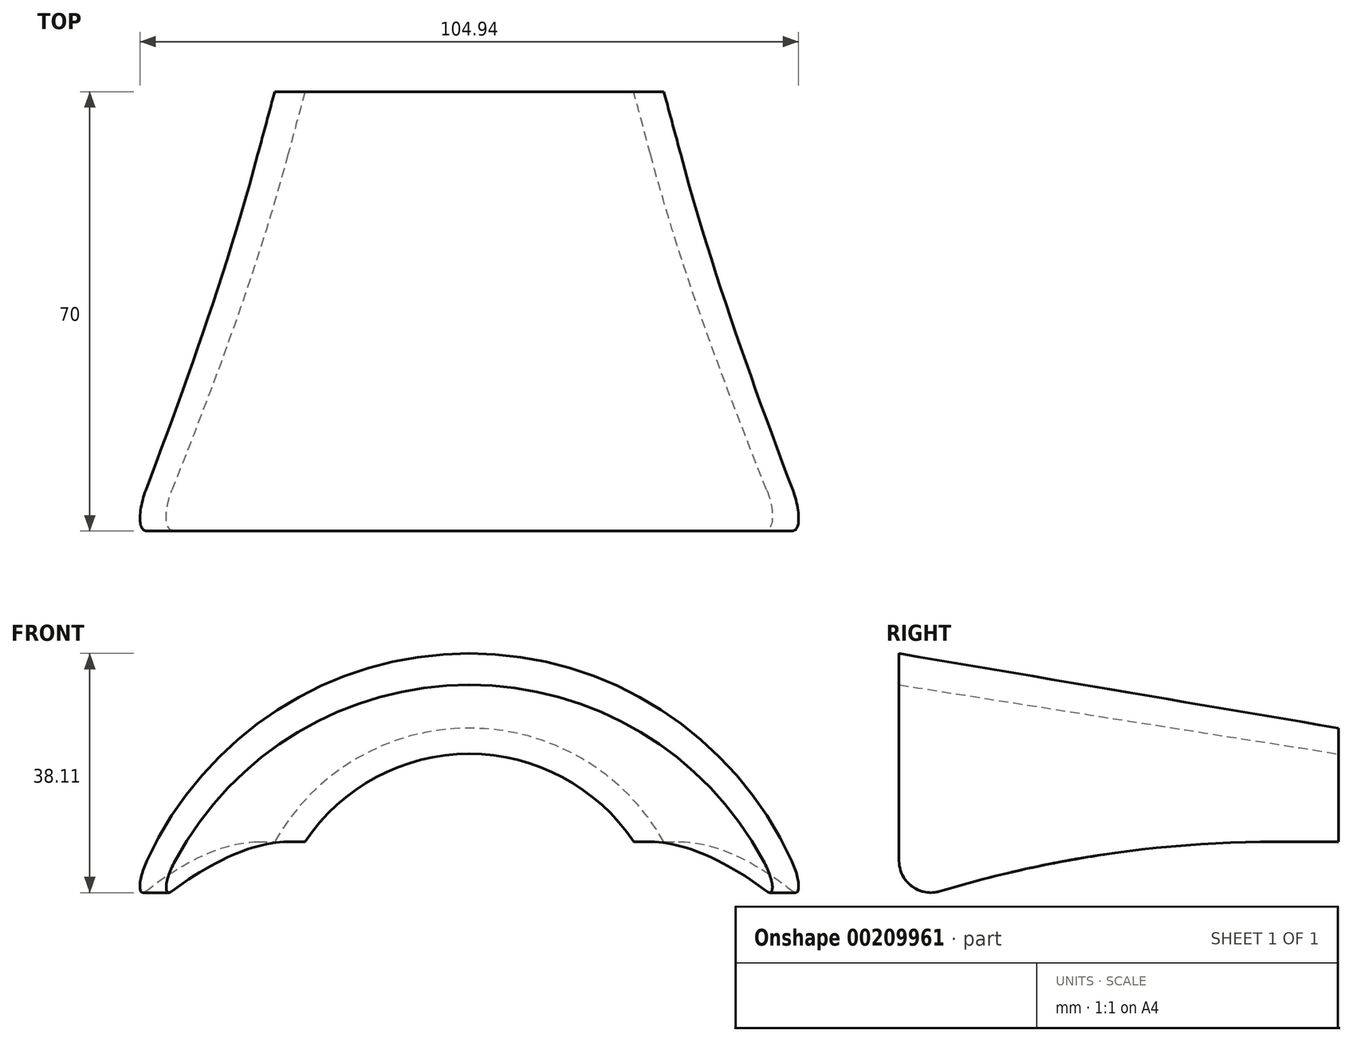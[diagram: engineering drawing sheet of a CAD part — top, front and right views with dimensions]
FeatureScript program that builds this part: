
annotation { "Feature Type Name" : "Feature", "Feature Type Description" : "" }
export const myFeature = defineFeature(function(context is Context, id is Id, definition is map)
    precondition{}
    {
        {
            var Q0;
            Q0=qCreatedBy(makeId("Front.planeOp"),FACE);
            cPlane(context, id + "F0", {"entities" : qUnion([Q0]), "cplaneType" : CPlaneType.OFFSET, "offset" : 35 * mm, "width" : 152.4 * mm, "height" : 152.4 * mm});
        }
        {
            var Q0;
            Q0=qCreatedBy(id+"F0.planeOp",FACE);
            var sketch = newSketch(context, id + "F1", { "sketchPlane" : qUnion([Q0])});
            skCircle(sketch, "E0", {"center": v(0, 0) * mm, "radius": 26.6 * mm, "construction": true});
            skLineSegment(sketch, "E1", {"start": v(-50, 0) * mm, "end": v(-54, 0) * mm});
            skLineSegment(sketch, "E2", {"start": v(50, 0) * mm, "end": v(54, 0) * mm});
            skArc(sketch, "E3", {"start": v(50, 0) * mm, "mid": v(0, 35) * mm, "end": v(-50, 0) * mm});
            skLineSegment(sketch, "E4", {"start": v(0, 0) * mm, "end": v(0, 35) * mm, "construction": true});
            skArc(sketch, "E5", {"start": v(54, 0) * mm, "mid": v(0, 40) * mm, "end": v(-54, 0) * mm});
            skLineSegment(sketch, "E6", {"start": v(0, 40) * mm, "end": v(0, 35) * mm, "construction": true});
            skSolve(sketch);
        }
        {
            var Q0;
            Q0=qCreatedBy(makeId("Front.planeOp"),FACE);
            cPlane(context, id + "F2", {"entities" : qUnion([Q0]), "cplaneType" : CPlaneType.OFFSET, "offset" : 35 * mm, "oppositeDirection" : true, "width" : 152.4 * mm, "height" : 152.4 * mm});
        }
        {
            var Q0;
            Q0=qCreatedBy(id+"F2.planeOp",FACE);
            var sketch = newSketch(context, id + "F3", { "sketchPlane" : qUnion([Q0])});
            skArc(sketch, "E7", {"start": v(26.6, 0) * mm, "mid": v(0, 26.6) * mm, "end": v(-26.6, 0) * mm, "construction": true});
            skCircle(sketch, "E8", {"center": v(0, 0) * mm, "radius": 45 * mm, "construction": true});
            skArc(sketch, "E9", {"start": v(30.6, 0) * mm, "mid": v(0, 30.6) * mm, "end": v(-30.6, 0) * mm, "construction": true});
            skLineSegment(sketch, "E10", {"start": v(26.6, 0) * mm, "end": v(30.6, 0) * mm, "construction": true});
            skLineSegment(sketch, "E11", {"start": v(-30.6, 0) * mm, "end": v(-26.6, 0) * mm, "construction": true});
            skArc(sketch, "E12", {"start": v(30.6, 0) * mm, "mid": v(0, 24) * mm, "end": v(-30.6, 0) * mm});
            skArc(sketch, "E13", {"start": v(34.81, 0) * mm, "mid": v(0, 28.1) * mm, "end": v(-34.81, 0) * mm});
            skLineSegment(sketch, "E14", {"start": v(-34.81, 0) * mm, "end": v(-30.6, 0) * mm});
            skLineSegment(sketch, "E15", {"start": v(30.6, 0) * mm, "end": v(34.81, 0) * mm});
            skLineSegment(sketch, "E16", {"start": v(0, 0) * mm, "end": v(0, 24) * mm, "construction": true});
            skSolve(sketch);
        }
        {
            var Q0;
            Q0=makeQuery(id+"F1.imprint","IMPRINT",FACE,{"disambiguationData":[TD([[makeQuery(id+"F1.imprint","IMPRINT",EDGE,{"derivedFrom":sQuery(id+"F1.wireOp",EDGE,"E1")}),-1.0]])]});
            var Q1;
            Q1=makeQuery(id+"F3.imprint","IMPRINT",FACE,{"disambiguationData":[TD([[makeQuery(id+"F3.imprint","IMPRINT",EDGE,{"derivedFrom":sQuery(id+"F3.wireOp",EDGE,"E12")}),-1.0]])]});
            var Q2;
            Q2=sQuery(id+"F3.wireOp",EDGE,"E9");
            var Q3;
            Q3=sQuery(id+"F3.wireOp",EDGE,"E7");
            var Q4;
            Q4=sQuery(id+"F3.wireOp",EDGE,"E11");
            var Q5;
            Q5=sQuery(id+"F3.wireOp",EDGE,"E10");
            loft(context, id + "F4", {"sheetProfilesArray" : [{ "sheetProfileEntities" : qUnion([Q0]) }, { "sheetProfileEntities" : qUnion([Q1]) }], "guidesArray" : [{ "guideEntities" : qUnion([Q2]), "guideDerivativeType" : LoftGuideDerivativeType.DEFAULT, "guideDerivativeMagnitude" : 1 }, { "guideEntities" : qUnion([Q3]), "guideDerivativeType" : LoftGuideDerivativeType.DEFAULT, "guideDerivativeMagnitude" : 1 }, { "guideEntities" : qUnion([Q4]), "guideDerivativeType" : LoftGuideDerivativeType.DEFAULT, "guideDerivativeMagnitude" : 1 }, { "guideEntities" : qUnion([Q5]), "guideDerivativeType" : LoftGuideDerivativeType.DEFAULT, "guideDerivativeMagnitude" : 1 }]});
        }
        {
            var Q0;
            Q0=qCreatedBy(makeId("Right.planeOp"),FACE);
            var sketch = newSketch(context, id + "F5", { "sketchPlane" : qUnion([Q0])});
            skLineSegment(sketch, "E17", {"start": v(35, 0) * mm, "end": v(35, 10) * mm});
            skLineSegment(sketch, "E18", {"start": v(-35, 0) * mm, "end": v(35, 0) * mm});
            skLineSegment(sketch, "E19", {"start": v(35, 10) * mm, "end": v(25, 10) * mm});
            skArc(sketch, "E20", {"start": v(25, 10) * mm, "mid": v(-5.41, 7.48) * mm, "end": v(-35, 0) * mm});
            skSolve(sketch);
        }
        {
            var Q0;
            Q0=makeQuery(id+"F5.imprint","IMPRINT",FACE,{"disambiguationData":[TD([[makeQuery(id+"F5.imprint","IMPRINT",EDGE,{"derivedFrom":sQuery(id+"F5.wireOp",EDGE,"E17")}),1.0]])]});
            extrude(context, id + "F6", {"entities" : qUnion([Q0]), "operationType" : NewBodyOperationType.REMOVE, "endBound" : BoundingType.SYMMETRIC, "oppositeDirection" : true, "depth" : 120 * mm});
        }
        {
            var Q0;
            Q0=makeQuery(id+"F6.boolean.opBoolean","MERGE",EDGE,{"derivedFrom":[makeQuery(id+"F4.opLoft","MID_CAP_EDGE",EDGE,{"disambiguationData":[OSD([sQuery(id+"F1.wireOp",EDGE,"E2"),sQuery(id+"F1.wireOp",EDGE,"E3"),sQuery(id+"F1.wireOp",EDGE,"E5")])],"capPos":0.0}),makeQuery(id+"F6.opExtrude","SWEPT_EDGE",EDGE,{"disambiguationData":[OSD([sQuery(id+"F5.wireOp",EDGE,"E18"),sQuery(id+"F5.wireOp",EDGE,"E20")])]})]});
            var Q1;
            Q1=makeQuery(id+"F6.boolean.opBoolean","MERGE",EDGE,{"derivedFrom":[makeQuery(id+"F4.opLoft","MID_CAP_EDGE",EDGE,{"disambiguationData":[OSD([sQuery(id+"F1.wireOp",EDGE,"E1"),sQuery(id+"F1.wireOp",EDGE,"E3"),sQuery(id+"F1.wireOp",EDGE,"E5")])],"capPos":0.0}),makeQuery(id+"F6.opExtrude","SWEPT_EDGE",EDGE,{"disambiguationData":[OSD([sQuery(id+"F5.wireOp",EDGE,"E18"),sQuery(id+"F5.wireOp",EDGE,"E20")])]})]});
            fillet(context, id + "F7", {"entities" : qUnion([Q0, Q1]), "radius" : 5.08 * mm, "tangentPropagation" : true, "allowEdgeOverflow" : false});
        }
    });
